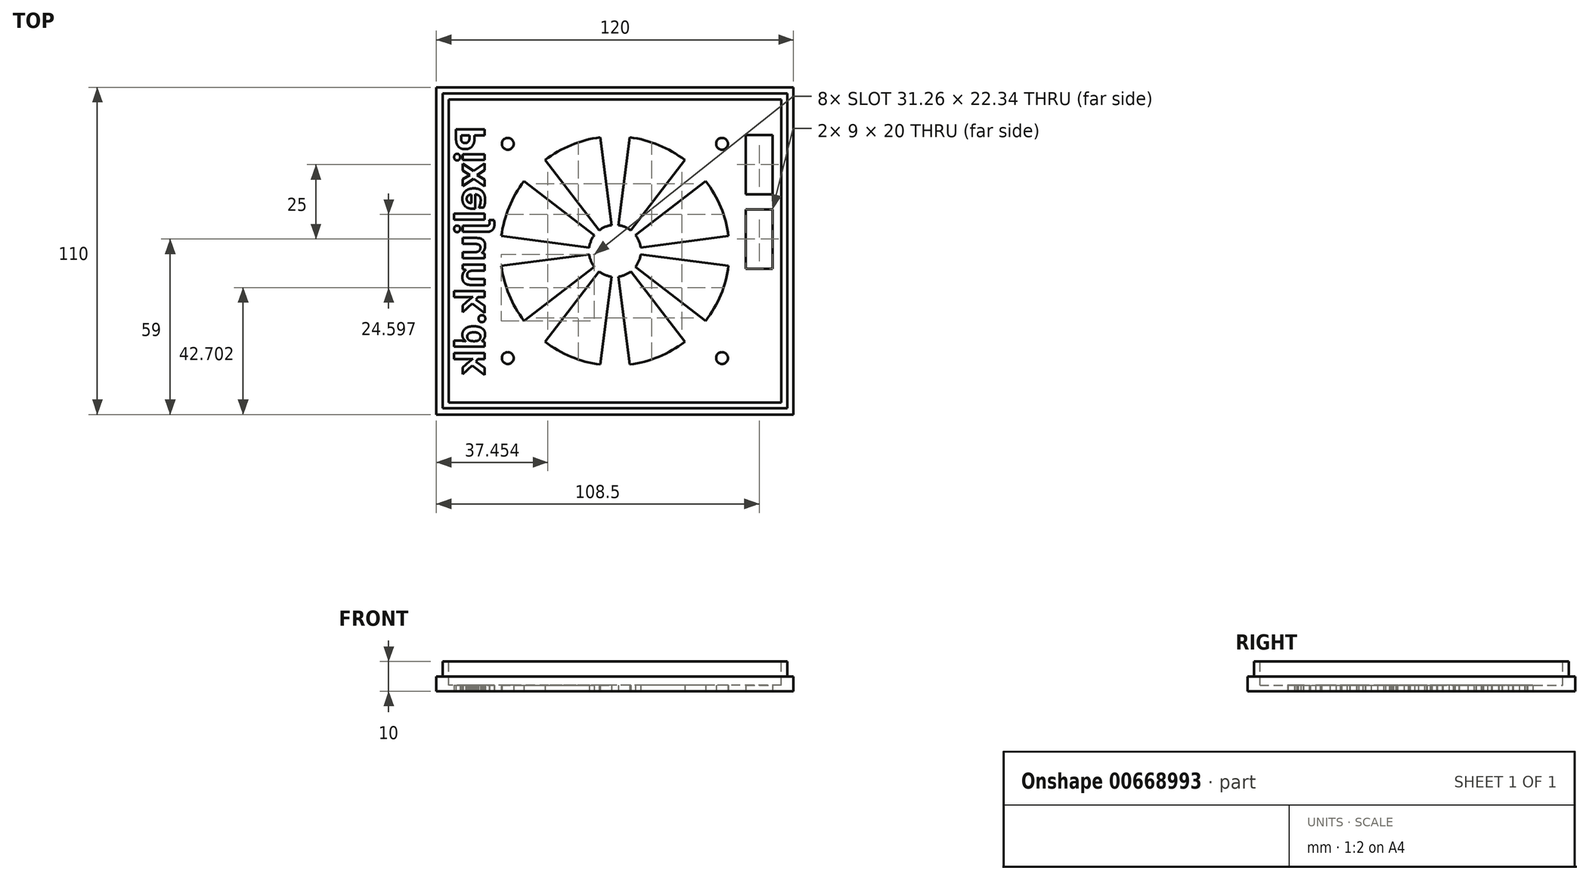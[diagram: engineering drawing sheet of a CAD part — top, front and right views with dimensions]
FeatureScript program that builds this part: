
annotation { "Feature Type Name" : "Feature", "Feature Type Description" : "" }
export const myFeature = defineFeature(function(context is Context, id is Id, definition is map)
    precondition{}
    {
        {
            var Q0;
            Q0=qCreatedBy(makeId("Top.planeOp"),FACE);
            var sketch = newSketch(context, id + "F0", { "sketchPlane" : qUnion([Q0])});
            skLineSegment(sketch, "E0.bottom", {"start": v(60, -55) * mm, "end": v(-60, -55) * mm});
            skLineSegment(sketch, "E0.top", {"start": v(60, 55) * mm, "end": v(-60, 55) * mm});
            skLineSegment(sketch, "E0.left", {"start": v(60, -55) * mm, "end": v(60, 55) * mm});
            skLineSegment(sketch, "E0.right", {"start": v(-60, -55) * mm, "end": v(-60, 55) * mm});
            skPoint(sketch, "E0.middle", {"position": v(0, 0) * mm});
            skSolve(sketch);
        }
        {
            var Q0;
            Q0 = qSketchRegion(id + "F0", true);
            extrude(context, id + "F1", {"entities" : qUnion([Q0]), "depth" : 5 * mm, "offsetDistance" : 25 * mm});
        }
        {
            var Q0;
            Q0=makeQuery(id+"F1.opExtrude","CAP_FACE",FACE,{"disambiguationData":[OSD([sQuery(id+"F0.wireOp",EDGE,"E0.bottom"),sQuery(id+"F0.wireOp",EDGE,"E0.top"),sQuery(id+"F0.wireOp",EDGE,"E0.left"),sQuery(id+"F0.wireOp",EDGE,"E0.right")])],"isStart":false});
            var sketch = newSketch(context, id + "F2", { "sketchPlane" : qUnion([Q0])});
            skLineSegment(sketch, "E1.bottom", {"start": v(57.9, -52.9) * mm, "end": v(-57.9, -52.9) * mm});
            skLineSegment(sketch, "E1.top", {"start": v(57.9, 52.9) * mm, "end": v(-57.9, 52.9) * mm});
            skLineSegment(sketch, "E1.left", {"start": v(57.9, -52.9) * mm, "end": v(57.9, 52.9) * mm});
            skLineSegment(sketch, "E1.right", {"start": v(-57.9, -52.9) * mm, "end": v(-57.9, 52.9) * mm});
            skPoint(sketch, "E1.middle", {"position": v(0, 0) * mm});
            skSolve(sketch);
        }
        {
            var Q0;
            Q0 = qSketchRegion(id + "F2", true);
            extrude(context, id + "F3", {"entities" : qUnion([Q0]), "operationType" : NewBodyOperationType.ADD, "depth" : 5 * mm, "offsetDistance" : 25 * mm});
        }
        {
            var Q0;
            Q0=makeQuery(id+"F3.opExtrude","CAP_FACE",FACE,{"disambiguationData":[OSD([sQuery(id+"F2.wireOp",EDGE,"E1.bottom"),sQuery(id+"F2.wireOp",EDGE,"E1.top"),sQuery(id+"F2.wireOp",EDGE,"E1.left"),sQuery(id+"F2.wireOp",EDGE,"E1.right")])],"isStart":false});
            var sketch = newSketch(context, id + "F4", { "sketchPlane" : qUnion([Q0])});
            skLineSegment(sketch, "E2.bottom", {"start": v(55.9, -50.9) * mm, "end": v(-55.9, -50.9) * mm});
            skLineSegment(sketch, "E2.top", {"start": v(55.9, 50.9) * mm, "end": v(-55.9, 50.9) * mm});
            skLineSegment(sketch, "E2.left", {"start": v(55.9, -50.9) * mm, "end": v(55.9, 50.9) * mm});
            skLineSegment(sketch, "E2.right", {"start": v(-55.9, -50.9) * mm, "end": v(-55.9, 50.9) * mm});
            skPoint(sketch, "E2.middle", {"position": v(0, 0) * mm});
            skSolve(sketch);
        }
        {
            var Q0;
            Q0 = qSketchRegion(id + "F4", true);
            extrude(context, id + "F5", {"entities" : qUnion([Q0]), "operationType" : NewBodyOperationType.REMOVE, "oppositeDirection" : true, "depth" : 8 * mm, "offsetDistance" : 25 * mm});
        }
        {
            var Q0;
            Q0=makeQuery(id+"F1.opExtrude","CAP_FACE",FACE,{"disambiguationData":[OSD([sQuery(id+"F0.wireOp",EDGE,"E0.bottom"),sQuery(id+"F0.wireOp",EDGE,"E0.top"),sQuery(id+"F0.wireOp",EDGE,"E0.left"),sQuery(id+"F0.wireOp",EDGE,"E0.right")])],"isStart":true});
            var sketch = newSketch(context, id + "F6", { "sketchPlane" : qUnion([Q0])});
            skLineSegment(sketch, "E3.bottom", {"start": v(-40, -40) * mm, "end": v(40, -40) * mm});
            skLineSegment(sketch, "E3.top", {"start": v(-40, 40) * mm, "end": v(40, 40) * mm});
            skLineSegment(sketch, "E3.left", {"start": v(-40, -40) * mm, "end": v(-40, 40) * mm});
            skLineSegment(sketch, "E3.right", {"start": v(40, -40) * mm, "end": v(40, 40) * mm});
            skPoint(sketch, "E3.middle", {"position": v(0, 0) * mm});
            skCircle(sketch, "E4", {"center": v(0, 0) * mm, "radius": 38.5 * mm});
            skCircle(sketch, "E5", {"center": v(36, 36) * mm, "radius": 2 * mm});
            skCircle(sketch, "E6.0.1.0", {"center": v(36, -36) * mm, "radius": 2 * mm});
            skCircle(sketch, "E6.1.0.0", {"center": v(-36, 36) * mm, "radius": 2 * mm});
            skCircle(sketch, "E6.1.1.0", {"center": v(-36, -36) * mm, "radius": 2 * mm});
            skLineSegment(sketch, "E6.direction1", {"start": v(36, 36) * mm, "end": v(-36, 36) * mm, "construction": true});
            skLineSegment(sketch, "E6.direction2", {"start": v(36, 36) * mm, "end": v(36, -36) * mm, "construction": true});
            skPoint(sketch, "E7.endSnap0", {"position": v(0, 36) * mm});
            skPoint(sketch, "E8.endSnap0", {"position": v(-40, 0) * mm});
            skPoint(sketch, "E9.endSnap0", {"position": v(40, 0) * mm});
            skLineSegment(sketch, "E10", {"start": v(0, 0) * mm, "end": v(-4.99, 38.18) * mm});
            skLineSegment(sketch, "E11", {"start": v(0, 0) * mm, "end": v(4.99, 38.18) * mm});
            skLineSegment(sketch, "E12.1.1", {"start": v(0, 0) * mm, "end": v(-23.47, 30.52) * mm});
            skLineSegment(sketch, "E12.1.2", {"start": v(0, 0) * mm, "end": v(-30.52, 23.47) * mm});
            skLineSegment(sketch, "E12.2.1", {"start": v(0, 0) * mm, "end": v(-38.18, 4.99) * mm});
            skLineSegment(sketch, "E12.2.2", {"start": v(0, 0) * mm, "end": v(-38.18, -4.99) * mm});
            skLineSegment(sketch, "E12.3.1", {"start": v(0, 0) * mm, "end": v(-30.52, -23.47) * mm});
            skLineSegment(sketch, "E12.3.2", {"start": v(0, 0) * mm, "end": v(-23.47, -30.52) * mm});
            skLineSegment(sketch, "E12.4.1", {"start": v(0, 0) * mm, "end": v(-4.99, -38.18) * mm});
            skLineSegment(sketch, "E12.4.2", {"start": v(0, 0) * mm, "end": v(4.99, -38.18) * mm});
            skLineSegment(sketch, "E12.5.1", {"start": v(0, 0) * mm, "end": v(23.47, -30.52) * mm});
            skLineSegment(sketch, "E12.5.2", {"start": v(0, 0) * mm, "end": v(30.52, -23.47) * mm});
            skLineSegment(sketch, "E12.6.1", {"start": v(0, 0) * mm, "end": v(38.18, -4.99) * mm});
            skLineSegment(sketch, "E12.6.2", {"start": v(0, 0) * mm, "end": v(38.18, 4.99) * mm});
            skLineSegment(sketch, "E12.7.1", {"start": v(0, 0) * mm, "end": v(30.52, 23.47) * mm});
            skLineSegment(sketch, "E12.7.2", {"start": v(0, 0) * mm, "end": v(23.47, 30.52) * mm});
            skCircle(sketch, "E13", {"center": v(0, 0) * mm, "radius": 8.72 * mm});
            skSolve(sketch);
        }
        {
            var Q0;
            {var subQ0=sQuery(id+"F6.wireOp",EDGE,"E10");var subQ1=sQuery(id+"F6.wireOp",EDGE,"E4");var subQ2=makeQuery(id+"F6.imprint","INTERSECT",VERTEX,{"derivedFrom":[subQ1,subQ0]});Q0=makeQuery(id+"F6.imprint","IMPRINT",FACE,{"disambiguationData":[TD([[makeQuery(id+"F6.imprint","IMPRINT",EDGE,{"disambiguationData":[TD([[subQ2,-1.0]])],"derivedFrom":subQ1}),1.0]])]});}
            var Q1;
            {var subQ0=sQuery(id+"F6.wireOp",EDGE,"E11");var subQ1=sQuery(id+"F6.wireOp",EDGE,"E4");var subQ2=makeQuery(id+"F6.imprint","INTERSECT",VERTEX,{"derivedFrom":[subQ1,subQ0]});Q1=makeQuery(id+"F6.imprint","IMPRINT",FACE,{"disambiguationData":[TD([[makeQuery(id+"F6.imprint","IMPRINT",EDGE,{"disambiguationData":[TD([[subQ2,1.0]])],"derivedFrom":subQ1}),1.0]])]});}
            var Q2;
            {var subQ0=sQuery(id+"F6.wireOp",EDGE,"E12.6.2");var subQ1=sQuery(id+"F6.wireOp",EDGE,"E4");var subQ2=makeQuery(id+"F6.imprint","INTERSECT",VERTEX,{"derivedFrom":[subQ1,subQ0]});Q2=makeQuery(id+"F6.imprint","IMPRINT",FACE,{"disambiguationData":[TD([[makeQuery(id+"F6.imprint","IMPRINT",EDGE,{"disambiguationData":[TD([[subQ2,-1.0]])],"derivedFrom":subQ1}),1.0]])]});}
            var Q3;
            {var subQ0=sQuery(id+"F6.wireOp",EDGE,"E12.5.2");var subQ1=sQuery(id+"F6.wireOp",EDGE,"E4");var subQ2=makeQuery(id+"F6.imprint","INTERSECT",VERTEX,{"derivedFrom":[subQ1,subQ0]});Q3=makeQuery(id+"F6.imprint","IMPRINT",FACE,{"disambiguationData":[TD([[makeQuery(id+"F6.imprint","IMPRINT",EDGE,{"disambiguationData":[TD([[subQ2,-1.0]])],"derivedFrom":subQ1}),1.0]])]});}
            var Q4;
            {var subQ0=sQuery(id+"F6.wireOp",EDGE,"E12.4.2");var subQ1=sQuery(id+"F6.wireOp",EDGE,"E4");var subQ2=makeQuery(id+"F6.imprint","INTERSECT",VERTEX,{"derivedFrom":[subQ1,subQ0]});Q4=makeQuery(id+"F6.imprint","IMPRINT",FACE,{"disambiguationData":[TD([[makeQuery(id+"F6.imprint","IMPRINT",EDGE,{"disambiguationData":[TD([[subQ2,-1.0]])],"derivedFrom":subQ1}),1.0]])]});}
            var Q5;
            {var subQ0=sQuery(id+"F6.wireOp",EDGE,"E12.3.2");var subQ1=sQuery(id+"F6.wireOp",EDGE,"E4");var subQ2=makeQuery(id+"F6.imprint","INTERSECT",VERTEX,{"derivedFrom":[subQ1,subQ0]});Q5=makeQuery(id+"F6.imprint","IMPRINT",FACE,{"disambiguationData":[TD([[makeQuery(id+"F6.imprint","IMPRINT",EDGE,{"disambiguationData":[TD([[subQ2,-1.0]])],"derivedFrom":subQ1}),1.0]])]});}
            var Q6;
            {var subQ0=sQuery(id+"F6.wireOp",EDGE,"E12.2.2");var subQ1=sQuery(id+"F6.wireOp",EDGE,"E4");var subQ2=makeQuery(id+"F6.imprint","INTERSECT",VERTEX,{"derivedFrom":[subQ1,subQ0]});Q6=makeQuery(id+"F6.imprint","IMPRINT",FACE,{"disambiguationData":[TD([[makeQuery(id+"F6.imprint","IMPRINT",EDGE,{"disambiguationData":[TD([[subQ2,-1.0]])],"derivedFrom":subQ1}),1.0]])]});}
            var Q7;
            {var subQ0=sQuery(id+"F6.wireOp",EDGE,"E12.1.2");var subQ1=sQuery(id+"F6.wireOp",EDGE,"E4");var subQ2=makeQuery(id+"F6.imprint","INTERSECT",VERTEX,{"derivedFrom":[subQ1,subQ0]});Q7=makeQuery(id+"F6.imprint","IMPRINT",FACE,{"disambiguationData":[TD([[makeQuery(id+"F6.imprint","IMPRINT",EDGE,{"disambiguationData":[TD([[subQ2,-1.0]])],"derivedFrom":subQ1}),1.0]])]});}
            var Q8;
            Q8=makeQuery(id+"F6.imprint","IMPRINT",FACE,{"disambiguationData":[TD([[makeQuery(id+"F6.imprint","IMPRINT",EDGE,{"derivedFrom":sQuery(id+"F6.wireOp",EDGE,"E5")}),1.0]])]});
            var Q9;
            Q9=makeQuery(id+"F6.imprint","IMPRINT",FACE,{"disambiguationData":[TD([[makeQuery(id+"F6.imprint","IMPRINT",EDGE,{"derivedFrom":sQuery(id+"F6.wireOp",EDGE,"E6.1.0.0")}),1.0]])]});
            var Q10;
            Q10=makeQuery(id+"F6.imprint","IMPRINT",FACE,{"disambiguationData":[TD([[makeQuery(id+"F6.imprint","IMPRINT",EDGE,{"derivedFrom":sQuery(id+"F6.wireOp",EDGE,"E6.1.1.0")}),1.0]])]});
            var Q11;
            Q11=makeQuery(id+"F6.imprint","IMPRINT",FACE,{"disambiguationData":[TD([[makeQuery(id+"F6.imprint","IMPRINT",EDGE,{"derivedFrom":sQuery(id+"F6.wireOp",EDGE,"E6.0.1.0")}),1.0]])]});
            extrude(context, id + "F7", {"entities" : qUnion([Q0, Q1, Q2, Q3, Q4, Q5, Q6, Q7, Q8, Q9, Q10, Q11]), "operationType" : NewBodyOperationType.REMOVE, "oppositeDirection" : true, "depth" : 25 * mm, "offsetDistance" : 25 * mm});
        }
        {
            var Q0;
            Q0=makeQuery(id+"F1.opExtrude","CAP_FACE",FACE,{"disambiguationData":[OSD([sQuery(id+"F0.wireOp",EDGE,"E0.bottom"),sQuery(id+"F0.wireOp",EDGE,"E0.top"),sQuery(id+"F0.wireOp",EDGE,"E0.left"),sQuery(id+"F0.wireOp",EDGE,"E0.right")])],"isStart":true});
            var sketch = newSketch(context, id + "F8", { "sketchPlane" : qUnion([Q0])});
            skLineSegment(sketch, "E14.bottom", {"start": v(53, -19) * mm, "end": v(44, -19) * mm});
            skLineSegment(sketch, "E14.top", {"start": v(53, -39) * mm, "end": v(44, -39) * mm});
            skLineSegment(sketch, "E14.left", {"start": v(53, -19) * mm, "end": v(53, -39) * mm});
            skLineSegment(sketch, "E14.right", {"start": v(44, -19) * mm, "end": v(44, -39) * mm});
            skPoint(sketch, "E14.middle", {"position": v(48.5, -29) * mm});
            skLineSegment(sketch, "E15.bottom", {"start": v(53, 6) * mm, "end": v(44, 6) * mm});
            skLineSegment(sketch, "E15.top", {"start": v(53, -14) * mm, "end": v(44, -14) * mm});
            skLineSegment(sketch, "E15.left", {"start": v(53, 6) * mm, "end": v(53, -14) * mm});
            skLineSegment(sketch, "E15.right", {"start": v(44, 6) * mm, "end": v(44, -14) * mm});
            skPoint(sketch, "E15.middle", {"position": v(48.5, -4) * mm});
            skSolve(sketch);
        }
        {
            var Q0;
            Q0=makeQuery(id+"F8.imprint","IMPRINT",FACE,{"disambiguationData":[TD([[makeQuery(id+"F8.imprint","IMPRINT",EDGE,{"derivedFrom":sQuery(id+"F8.wireOp",EDGE,"E15.bottom")}),1.0]])]});
            var Q1;
            Q1=makeQuery(id+"F8.imprint","IMPRINT",FACE,{"disambiguationData":[TD([[makeQuery(id+"F8.imprint","IMPRINT",EDGE,{"derivedFrom":sQuery(id+"F8.wireOp",EDGE,"E14.bottom")}),1.0]])]});
            extrude(context, id + "F9", {"entities" : qUnion([Q0, Q1]), "operationType" : NewBodyOperationType.REMOVE, "oppositeDirection" : true, "depth" : 25 * mm, "offsetDistance" : 25 * mm});
        }
        {
            var Q0;
            Q0=makeQuery(id+"F1.opExtrude","CAP_FACE",FACE,{"disambiguationData":[OSD([sQuery(id+"F0.wireOp",EDGE,"E0.bottom"),sQuery(id+"F0.wireOp",EDGE,"E0.top"),sQuery(id+"F0.wireOp",EDGE,"E0.left"),sQuery(id+"F0.wireOp",EDGE,"E0.right")])],"isStart":true});
            var sketch = newSketch(context, id + "F10", { "sketchPlane" : qUnion([Q0])});
            skText(sketch, "E16", { "text": "Pixeljunk.dk", "fontName": "OpenSans-Bold.ttf"});
            const initialGuessF10  = {"E16": [-0.04374, -0.0421, 0, 1, 0.00975]};
            skSetInitialGuess(sketch, initialGuessF10);
            skSolve(sketch);
        }
        {
            var Q0;
            Q0 = qSketchRegion(id + "F10", true);
            extrude(context, id + "F11", {"entities" : qUnion([Q0]), "operationType" : NewBodyOperationType.REMOVE, "oppositeDirection" : true, "depth" : 25 * mm, "offsetDistance" : 25 * mm});
        }
    });
